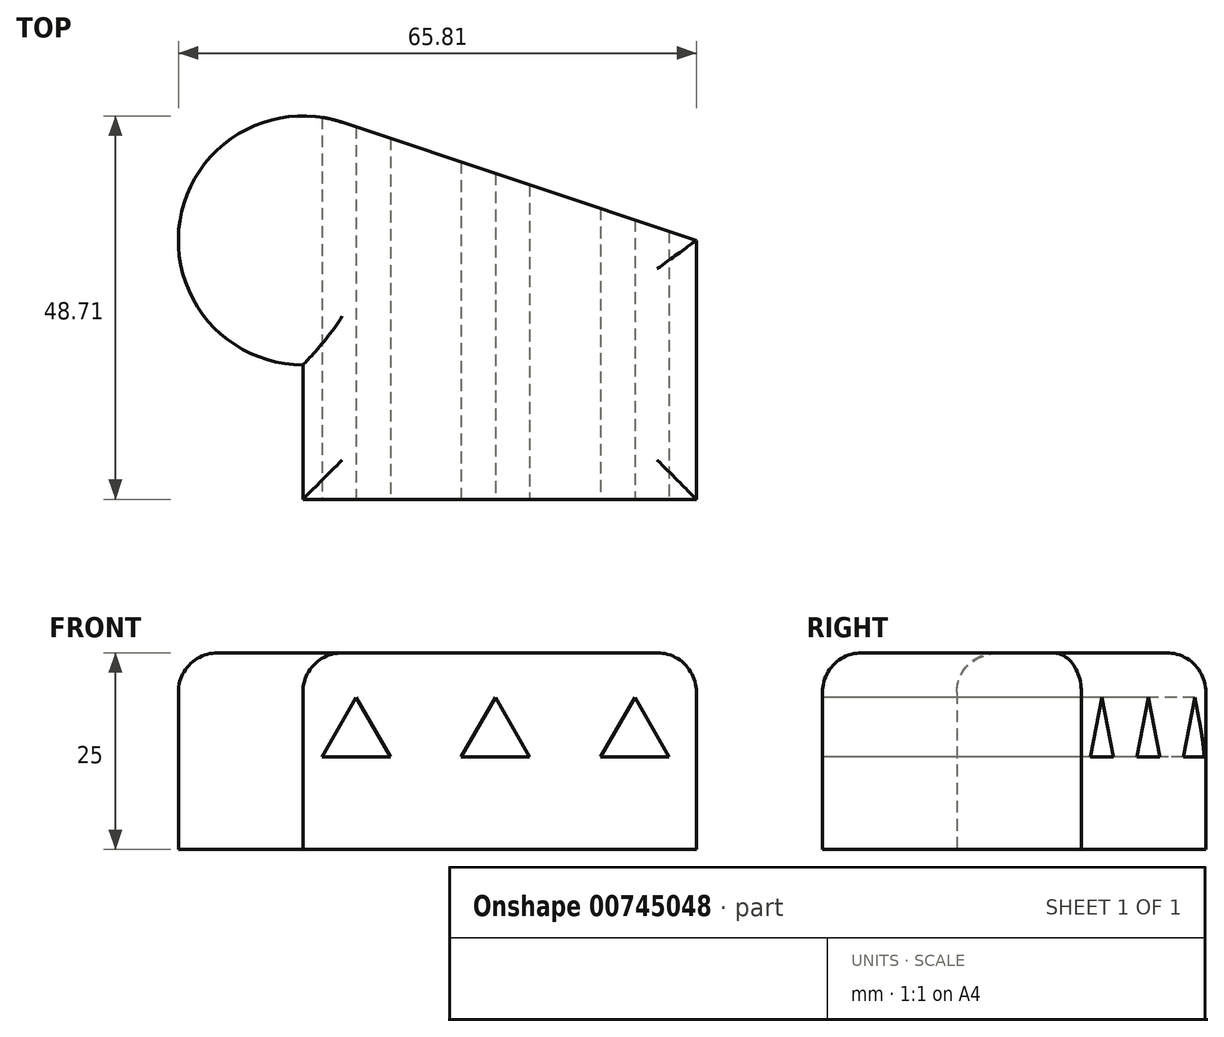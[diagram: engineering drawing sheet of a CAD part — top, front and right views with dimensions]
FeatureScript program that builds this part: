
annotation { "Feature Type Name" : "Feature", "Feature Type Description" : "" }
export const myFeature = defineFeature(function(context is Context, id is Id, definition is map)
    precondition{}
    {
        {
            var Q0;
            Q0=qCreatedBy(makeId("Top.planeOp"),FACE);
            var sketch = newSketch(context, id + "F0", { "sketchPlane" : qUnion([Q0])});
            skLineSegment(sketch, "E0.bottom", {"start": v(-24.45, 15.07) * mm, "end": v(25.55, 15.07) * mm});
            skLineSegment(sketch, "E0.top", {"start": v(-24.45, -17.82) * mm, "end": v(25.55, -17.82) * mm});
            skLineSegment(sketch, "E0.left", {"start": v(-24.45, 15.07) * mm, "end": v(-24.45, -17.82) * mm});
            skLineSegment(sketch, "E0.right", {"start": v(25.55, 15.07) * mm, "end": v(25.55, -17.82) * mm});
            skCircle(sketch, "E1", {"center": v(-24.45, 15.07) * mm, "radius": 15.82 * mm});
            skLineSegment(sketch, "E2", {"start": v(-19.44, 30.08) * mm, "end": v(25.55, 15.07) * mm});
            skCircle(sketch, "E3", {"center": v(-24.45, 15.07) * mm, "radius": 6.61 * mm});
            skSolve(sketch);
        }
        {
            var Q0;
            {var subQ0=sQuery(id+"F0.wireOp",EDGE,"E3");var subQ1=sQuery(id+"F0.wireOp",EDGE,"E0.bottom");var subQ2=makeQuery(id+"F0.imprint","INTERSECT",VERTEX,{"derivedFrom":[subQ1,subQ0]});Q0=makeQuery(id+"F0.imprint","IMPRINT",FACE,{"disambiguationData":[TD([[makeQuery(id+"F0.imprint","IMPRINT",EDGE,{"disambiguationData":[TD([[subQ2,-1.0]])],"derivedFrom":subQ1}),1.0]])]});}
            var Q1;
            {var subQ0=sQuery(id+"F0.wireOp",EDGE,"E0.left");var subQ1=sQuery(id+"F0.wireOp",EDGE,"E0.bottom");var subQ2=makeQuery(id+"F0.imprint","INTERSECT",VERTEX,{"derivedFrom":[subQ1,subQ0]});Q1=makeQuery(id+"F0.imprint","IMPRINT",FACE,{"disambiguationData":[TD([[makeQuery(id+"F0.imprint","IMPRINT",EDGE,{"disambiguationData":[TD([[subQ2,-1.0]])],"derivedFrom":subQ1}),-1.0]])]});}
            var Q2;
            {var subQ0=sQuery(id+"F0.wireOp",EDGE,"E0.left");var subQ1=sQuery(id+"F0.wireOp",EDGE,"E0.bottom");var subQ2=makeQuery(id+"F0.imprint","INTERSECT",VERTEX,{"derivedFrom":[subQ1,subQ0]});Q2=makeQuery(id+"F0.imprint","IMPRINT",FACE,{"disambiguationData":[TD([[makeQuery(id+"F0.imprint","IMPRINT",EDGE,{"disambiguationData":[TD([[subQ2,-1.0]])],"derivedFrom":subQ1}),1.0]])]});}
            var Q3;
            {var subQ0=sQuery(id+"F0.wireOp",EDGE,"E2");Q3=makeQuery(id+"F0.imprint","IMPRINT",FACE,{"disambiguationData":[TD([[makeQuery(id+"F0.imprint","IMPRINT",EDGE,{"derivedFrom":subQ0}),-1.0]])]});}
            var Q4;
            {var subQ1=sQuery(id+"F0.wireOp",EDGE,"E0.top");Q4=makeQuery(id+"F0.imprint","IMPRINT",FACE,{"disambiguationData":[TD([[makeQuery(id+"F0.imprint","IMPRINT",EDGE,{"derivedFrom":subQ1}),1.0]])]});}
            var Q5;
            {var subQ0=sQuery(id+"F0.wireOp",EDGE,"E3");var subQ1=sQuery(id+"F0.wireOp",EDGE,"E0.bottom");var subQ2=makeQuery(id+"F0.imprint","INTERSECT",VERTEX,{"derivedFrom":[subQ1,subQ0]});Q5=makeQuery(id+"F0.imprint","IMPRINT",FACE,{"disambiguationData":[TD([[makeQuery(id+"F0.imprint","IMPRINT",EDGE,{"disambiguationData":[TD([[subQ2,-1.0]])],"derivedFrom":subQ1}),-1.0]])]});}
            extrude(context, id + "F1", {"entities" : qUnion([Q0, Q1, Q2, Q3, Q4, Q5]), "depth" : 25 * mm, "offsetDistance" : 25 * mm});
        }
        {
            var Q0;
            Q0=sQuery(id+"F0.wireOp",EDGE,"E3");
            extrude(context, id + "F2", {"bodyType" : ToolBodyType.SURFACE, "surfaceEntities" : qUnion([Q0]), "endBound" : BoundingType.SYMMETRIC, "depth" : 90.2 * mm, "offsetDistance" : 25 * mm});
        }
        {
            var Q0;
            Q0=makeQuery(id+"F1.opExtrude","SWEPT_FACE",FACE,{"disambiguationData":[OSD([sQuery(id+"F0.wireOp",EDGE,"E0.top")])]});
            var sketch = newSketch(context, id + "F3", { "sketchPlane" : qUnion([Q0])});
            skPoint(sketch, "E4.cCircle.centerSnap0", {"position": v(-24.45, 12.5) * mm});
            skCircle(sketch, "E5.cCircle", {"center": v(-17.68, 14.3) * mm, "radius": 2.51 * mm, "construction": true});
            skLineSegment(sketch, "E5.0", {"start": v(-13.33, 11.79) * mm, "end": v(-22.03, 11.79) * mm});
            skLineSegment(sketch, "E5.1", {"start": v(-22.03, 11.79) * mm, "end": v(-17.68, 19.33) * mm});
            skLineSegment(sketch, "E5.2", {"start": v(-17.68, 19.33) * mm, "end": v(-13.33, 11.79) * mm});
            skPoint(sketch, "E5.0.midPoint", {"position": v(-17.68, 11.79) * mm});
            skLineSegment(sketch, "E6.1.0.0", {"start": v(0.02, 19.33) * mm, "end": v(4.37, 11.79) * mm});
            skCircle(sketch, "E6.1.0.1", {"center": v(0.02, 14.3) * mm, "radius": 2.51 * mm, "construction": true});
            skPoint(sketch, "E6.1.0.2", {"position": v(-6.75, 12.5) * mm});
            skLineSegment(sketch, "E6.1.0.3", {"start": v(4.37, 11.79) * mm, "end": v(-4.33, 11.79) * mm});
            skPoint(sketch, "E6.1.0.4", {"position": v(0.02, 11.79) * mm});
            skLineSegment(sketch, "E6.1.0.5", {"start": v(-4.33, 11.79) * mm, "end": v(0.02, 19.33) * mm});
            skLineSegment(sketch, "E6.2.0.0", {"start": v(17.72, 19.33) * mm, "end": v(22.07, 11.79) * mm});
            skCircle(sketch, "E6.2.0.1", {"center": v(17.72, 14.3) * mm, "radius": 2.51 * mm, "construction": true});
            skPoint(sketch, "E6.2.0.2", {"position": v(10.95, 12.5) * mm});
            skLineSegment(sketch, "E6.2.0.3", {"start": v(22.07, 11.79) * mm, "end": v(13.37, 11.79) * mm});
            skPoint(sketch, "E6.2.0.4", {"position": v(17.72, 11.79) * mm});
            skLineSegment(sketch, "E6.2.0.5", {"start": v(13.37, 11.79) * mm, "end": v(17.72, 19.33) * mm});
            skLineSegment(sketch, "E6.direction1", {"start": v(-24.45, 12.5) * mm, "end": v(-6.75, 12.5) * mm, "construction": true});
            skSolve(sketch);
        }
        {
            var Q0;
            Q0=makeQuery(id+"F3.imprint","IMPRINT",FACE,{"disambiguationData":[TD([[makeQuery(id+"F3.imprint","IMPRINT",EDGE,{"derivedFrom":sQuery(id+"F3.wireOp",EDGE,"E5.0")}),-1.0]])]});
            var Q1;
            Q1=makeQuery(id+"F3.imprint","IMPRINT",FACE,{"disambiguationData":[TD([[makeQuery(id+"F3.imprint","IMPRINT",EDGE,{"derivedFrom":sQuery(id+"F3.wireOp",EDGE,"E6.1.0.0")}),-1.0]])]});
            var Q2;
            Q2=makeQuery(id+"F3.imprint","IMPRINT",FACE,{"disambiguationData":[TD([[makeQuery(id+"F3.imprint","IMPRINT",EDGE,{"derivedFrom":sQuery(id+"F3.wireOp",EDGE,"E6.2.0.0")}),-1.0]])]});
            extrude(context, id + "F4", {"entities" : qUnion([Q0, Q1, Q2]), "operationType" : NewBodyOperationType.REMOVE, "oppositeDirection" : true, "depth" : 25 * mm, "offsetDistance" : 25 * mm});
        }
        {
            var Q0;
            Q0=makeQuery(id+"F4.boolean.opBoolean","COPY",FACE,{"derivedFrom":makeQuery(id+"F4.opExtrude","CAP_FACE",FACE,{"disambiguationData":[OSD([sQuery(id+"F3.wireOp",EDGE,"E5.0"),sQuery(id+"F3.wireOp",EDGE,"E5.1"),sQuery(id+"F3.wireOp",EDGE,"E5.2")])],"isStart":false})});
            var Q1;
            Q1=makeQuery(id+"F4.boolean.opBoolean","COPY",FACE,{"derivedFrom":makeQuery(id+"F4.opExtrude","CAP_FACE",FACE,{"disambiguationData":[OSD([sQuery(id+"F3.wireOp",EDGE,"E6.1.0.0"),sQuery(id+"F3.wireOp",EDGE,"E6.1.0.3"),sQuery(id+"F3.wireOp",EDGE,"E6.1.0.5")])],"isStart":false})});
            var Q2;
            Q2=makeQuery(id+"F4.boolean.opBoolean","COPY",FACE,{"derivedFrom":makeQuery(id+"F4.opExtrude","CAP_FACE",FACE,{"disambiguationData":[OSD([sQuery(id+"F3.wireOp",EDGE,"E6.2.0.0"),sQuery(id+"F3.wireOp",EDGE,"E6.2.0.3"),sQuery(id+"F3.wireOp",EDGE,"E6.2.0.5")])],"isStart":false})});
            extrude(context, id + "F5", {"entities" : qUnion([Q0, Q1, Q2]), "operationType" : NewBodyOperationType.REMOVE, "endBound" : BoundingType.THROUGH_ALL, "oppositeDirection" : true, "depth" : 25 * mm, "offsetDistance" : 25 * mm});
        }
        {
            var Q0;
            Q0=makeQuery(id+"F1.opExtrude","CAP_FACE",FACE,{"disambiguationData":[OSD([sQuery(id+"F0.wireOp",EDGE,"E0.top"),sQuery(id+"F0.wireOp",EDGE,"E0.left"),sQuery(id+"F0.wireOp",EDGE,"E0.right"),sQuery(id+"F0.wireOp",EDGE,"E2"),sQuery(id+"F0.wireOp",EDGE,"E1")])],"isStart":false});
            fillet(context, id + "F6", {"entities" : qUnion([Q0]), "radius" : 5 * mm, "tangentPropagation" : true, "allowEdgeOverflow" : false});
        }
    });
